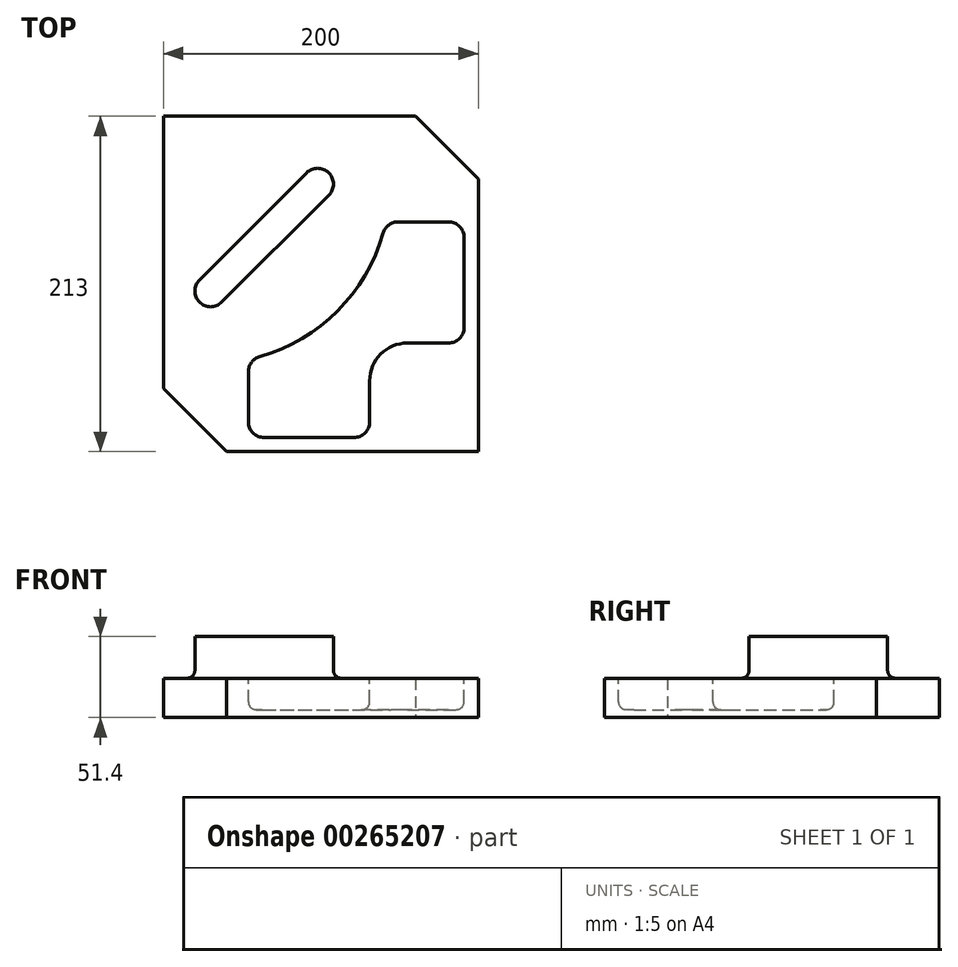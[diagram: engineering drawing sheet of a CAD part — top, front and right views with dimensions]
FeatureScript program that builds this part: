
annotation { "Feature Type Name" : "Feature", "Feature Type Description" : "" }
export const myFeature = defineFeature(function(context is Context, id is Id, definition is map)
    precondition{}
    {
        {
            var Q0;
            Q0=qCreatedBy(makeId("Top.planeOp"),FACE);
            var sketch = newSketch(context, id + "F0", { "sketchPlane" : qUnion([Q0])});
            skLineSegment(sketch, "E0.bottom", {"start": v(-69.1, -90.19) * mm, "end": v(90.9, -90.19) * mm});
            skLineSegment(sketch, "E0.right", {"start": v(90.9, -90.19) * mm, "end": v(90.9, 79.81) * mm});
            skArc(sketch, "E1", {"start": v(-86.16, 18.89) * mm, "mid": v(-86.16, 4.74) * mm, "end": v(-72.02, 4.74) * mm});
            skArc(sketch, "E2", {"start": v(-4.02, 72.74) * mm, "mid": v(-4.02, 86.89) * mm, "end": v(-18.16, 86.89) * mm});
            skArc(sketch, "E3", {"start": v(2.35, 65) * mm, "mid": v(3.39, 93.61) * mm, "end": v(-25.23, 93.96) * mm});
            skLineSegment(sketch, "E4", {"start": v(-93.23, 25.96) * mm, "end": v(-25.23, 93.96) * mm});
            skLineSegment(sketch, "E5", {"start": v(2.35, 65) * mm, "end": v(-64.95, -2.32) * mm});
            skLineSegment(sketch, "E6", {"start": v(-18.16, 86.89) * mm, "end": v(-86.16, 18.89) * mm});
            skLineSegment(sketch, "E7", {"start": v(-72.02, 4.74) * mm, "end": v(-4.02, 72.74) * mm});
            skArc(sketch, "E8.trimOffspring", {"start": v(-93.23, 25.96) * mm, "mid": v(-93.23, -2.33) * mm, "end": v(-64.95, -2.32) * mm});
            skLineSegment(sketch, "E9.bottom", {"start": v(90.9, -90.19) * mm, "end": v(-69.1, -90.19) * mm});
            skLineSegment(sketch, "E9.top", {"start": v(50.9, 122.81) * mm, "end": v(-109.1, 122.81) * mm});
            skLineSegment(sketch, "E9.left", {"start": v(90.9, 79.81) * mm, "end": v(90.9, 82.81) * mm});
            skLineSegment(sketch, "E9.right", {"start": v(-109.1, -50.19) * mm, "end": v(-109.1, 122.81) * mm});
            skLineSegment(sketch, "E10", {"start": v(90.9, 82.81) * mm, "end": v(50.9, 122.81) * mm});
            skPoint(sketch, "E11.orphan", {"position": v(90.9, 122.81) * mm});
            skLineSegment(sketch, "E12", {"start": v(-69.1, -90.19) * mm, "end": v(-109.1, -50.19) * mm});
            skPoint(sketch, "E13.orphan", {"position": v(-79.1, -90.19) * mm});
            skPoint(sketch, "E14.orphan", {"position": v(-109.1, -90.19) * mm});
            skArc(sketch, "E15", {"start": v(-47.83, -29.82) * mm, "mid": v(1.52, -0.8) * mm, "end": v(30.54, 48.56) * mm});
            skLineSegment(sketch, "E16", {"start": v(-55.1, -71.19) * mm, "end": v(-55.1, -39.43) * mm});
            skLineSegment(sketch, "E17", {"start": v(-45.1, -81.19) * mm, "end": v(11.9, -81.19) * mm});
            skLineSegment(sketch, "E18", {"start": v(21.9, -71.19) * mm, "end": v(21.9, -45.19) * mm});
            skLineSegment(sketch, "E19", {"start": v(45.9, -21.19) * mm, "end": v(71.9, -21.19) * mm});
            skLineSegment(sketch, "E20", {"start": v(81.9, -11.19) * mm, "end": v(81.9, 45.81) * mm});
            skLineSegment(sketch, "E21", {"start": v(71.9, 55.81) * mm, "end": v(40.16, 55.81) * mm});
            skPoint(sketch, "E22.visualSharp", {"position": v(21.9, -21.19) * mm});
            skArc(sketch, "E22.filletArc", {"start": v(45.9, -21.19) * mm, "mid": v(28.94, -28.21) * mm, "end": v(21.9, -45.19) * mm});
            skPoint(sketch, "E23.visualSharp", {"position": v(32.36, 55.81) * mm});
            skArc(sketch, "E23.filletArc", {"start": v(40.16, 55.81) * mm, "mid": v(34.13, 53.8) * mm, "end": v(30.54, 48.56) * mm});
            skPoint(sketch, "E24.visualSharp", {"position": v(81.9, 55.81) * mm});
            skArc(sketch, "E24.filletArc", {"start": v(81.9, 45.81) * mm, "mid": v(78.98, 52.89) * mm, "end": v(71.9, 55.81) * mm});
            skPoint(sketch, "E25.visualSharp", {"position": v(81.9, -21.19) * mm});
            skArc(sketch, "E25.filletArc", {"start": v(71.9, -21.19) * mm, "mid": v(78.98, -18.26) * mm, "end": v(81.9, -11.19) * mm});
            skPoint(sketch, "E26.visualSharp", {"position": v(21.9, -81.19) * mm});
            skArc(sketch, "E26.filletArc", {"start": v(11.9, -81.19) * mm, "mid": v(18.98, -78.26) * mm, "end": v(21.9, -71.19) * mm});
            skPoint(sketch, "E27.visualSharp", {"position": v(-55.1, -81.19) * mm});
            skArc(sketch, "E27.filletArc", {"start": v(-55.1, -71.19) * mm, "mid": v(-52.16, -78.26) * mm, "end": v(-45.1, -81.19) * mm});
            skPoint(sketch, "E28.visualSharp", {"position": v(-55.1, -31.63) * mm});
            skArc(sketch, "E28.filletArc", {"start": v(-47.83, -29.82) * mm, "mid": v(-53.07, -33.4) * mm, "end": v(-55.1, -39.43) * mm});
            skSolve(sketch);
        }
        {
            var Q0;
            Q0=makeQuery(id+"F0.imprint","IMPRINT",FACE,{"disambiguationData":[TD([[makeQuery(id+"F0.imprint","IMPRINT",EDGE,{"derivedFrom":sQuery(id+"F0.wireOp",EDGE,"E1")}),-1.0]])]});
            var Q1;
            Q1=makeQuery(id+"F0.imprint","IMPRINT",FACE,{"disambiguationData":[TD([[makeQuery(id+"F0.imprint","IMPRINT",EDGE,{"derivedFrom":sQuery(id+"F0.wireOp",EDGE,"E0.right")}),1.0]])]});
            var Q2;
            Q2=makeQuery(id+"F0.imprint","IMPRINT",FACE,{"disambiguationData":[TD([[makeQuery(id+"F0.imprint","IMPRINT",EDGE,{"derivedFrom":sQuery(id+"F0.wireOp",EDGE,"E15")}),-1.0]])]});
            var Q3;
            Q3=makeQuery(id+"F0.imprint","IMPRINT",FACE,{"disambiguationData":[TD([[makeQuery(id+"F0.imprint","IMPRINT",EDGE,{"derivedFrom":sQuery(id+"F0.wireOp",EDGE,"E1")}),1.0]])]});
            extrude(context, id + "F1", {"entities" : qUnion([Q0, Q1, Q2, Q3]), "depth" : 25 * mm});
        }
        {
            var Q0;
            Q0=makeQuery(id+"F0.imprint","IMPRINT",FACE,{"disambiguationData":[TD([[makeQuery(id+"F0.imprint","IMPRINT",EDGE,{"derivedFrom":sQuery(id+"F0.wireOp",EDGE,"E1")}),1.0]])]});
            extrude(context, id + "F2", {"entities" : qUnion([Q0]), "operationType" : NewBodyOperationType.ADD, "depth" : 51.4 * mm});
        }
        {
            var Q0;
            Q0=makeQuery(id+"F2.boolean.opBoolean","INTERSECT",EDGE,{"derivedFrom":[makeQuery(id+"F1.opExtrude","CAP_FACE",FACE,{"disambiguationData":[OSD([sQuery(id+"F0.wireOp",EDGE,"E0.right"),sQuery(id+"F0.wireOp",EDGE,"E9.bottom"),sQuery(id+"F0.wireOp",EDGE,"E9.top"),sQuery(id+"F0.wireOp",EDGE,"E9.left"),sQuery(id+"F0.wireOp",EDGE,"E9.right"),sQuery(id+"F0.wireOp",EDGE,"E10"),sQuery(id+"F0.wireOp",EDGE,"E12")])],"isStart":false}),makeQuery(id+"F2.opExtrude","SWEPT_FACE",FACE,{"disambiguationData":[OSD([sQuery(id+"F0.wireOp",EDGE,"E7")])]})]});
            fillet(context, id + "F3", {"entities" : qUnion([Q0]), "radius" : 5 * mm, "tangentPropagation" : true, "allowEdgeOverflow" : false});
        }
        {
            var Q0;
            Q0=makeQuery(id+"F0.imprint","IMPRINT",FACE,{"disambiguationData":[TD([[makeQuery(id+"F0.imprint","IMPRINT",EDGE,{"derivedFrom":sQuery(id+"F0.wireOp",EDGE,"E15")}),-1.0]])]});
            extrude(context, id + "F4", {"entities" : qUnion([Q0]), "operationType" : NewBodyOperationType.ADD, "depth" : 26 * mm});
        }
        {
            var Q0;
            Q0=makeQuery(id+"F4.opExtrude","CAP_FACE",FACE,{"disambiguationData":[OSD([sQuery(id+"F0.wireOp",EDGE,"E15"),sQuery(id+"F0.wireOp",EDGE,"E16"),sQuery(id+"F0.wireOp",EDGE,"E17"),sQuery(id+"F0.wireOp",EDGE,"E18"),sQuery(id+"F0.wireOp",EDGE,"E19"),sQuery(id+"F0.wireOp",EDGE,"E20"),sQuery(id+"F0.wireOp",EDGE,"E21"),sQuery(id+"F0.wireOp",EDGE,"E22.filletArc"),sQuery(id+"F0.wireOp",EDGE,"E23.filletArc"),sQuery(id+"F0.wireOp",EDGE,"E24.filletArc"),sQuery(id+"F0.wireOp",EDGE,"E25.filletArc"),sQuery(id+"F0.wireOp",EDGE,"E26.filletArc"),sQuery(id+"F0.wireOp",EDGE,"E27.filletArc"),sQuery(id+"F0.wireOp",EDGE,"E28.filletArc")])],"isStart":false});
            extrude(context, id + "F5", {"entities" : qUnion([Q0]), "operationType" : NewBodyOperationType.REMOVE, "oppositeDirection" : true, "depth" : 21 * mm});
        }
        {
            var Q0;
            Q0=makeQuery(id+"F4.boolean.opBoolean","INTERSECT",EDGE,{"derivedFrom":[makeQuery(id+"F1.opExtrude","CAP_FACE",FACE,{"disambiguationData":[OSD([sQuery(id+"F0.wireOp",EDGE,"E0.right"),sQuery(id+"F0.wireOp",EDGE,"E9.bottom"),sQuery(id+"F0.wireOp",EDGE,"E9.top"),sQuery(id+"F0.wireOp",EDGE,"E9.left"),sQuery(id+"F0.wireOp",EDGE,"E9.right"),sQuery(id+"F0.wireOp",EDGE,"E10"),sQuery(id+"F0.wireOp",EDGE,"E12")])],"isStart":false}),makeQuery(id+"F4.opExtrude","SWEPT_FACE",FACE,{"disambiguationData":[OSD([sQuery(id+"F0.wireOp",EDGE,"E15")])]})]});
            var Q1;
            Q1=makeQuery(id+"F5.boolean.opBoolean","COPY",EDGE,{"derivedFrom":makeQuery(id+"F5.opExtrude","CAP_EDGE",EDGE,{"disambiguationData":[OSD([sQuery(id+"F0.wireOp",EDGE,"E15")])],"isStart":false})});
            fillet(context, id + "F6", {"entities" : qUnion([Q0, Q1]), "radius" : 5 * mm, "tangentPropagation" : true, "allowEdgeOverflow" : false});
        }
    });
